# Revit family: PRD_FrankeWS_DspslChts_CHRONOSWasteDisposalChute_E-BS602E
name_source: partatom
category: Specialty Equipment
revit_build: Autodesk Revit 2018 (Build: 20190510_1515(x64)
units: mm (PartAtom-declared; Revit-internal decimal feet)

## family parameters
Cut with Voids When Loaded = No
Host = Face
OmniClass Number = 23.45.05.14.99
OmniClass Title = Other Sanitary Washing Plumbing Fixtures
Part Type = Normal
Room Calculation Point = No
Round Connector Dimension = Use Diameter
Shared = No

## types (1)
- E-BS602E
    AssetType = Fixed
    BIMObjectName = PRD_AR_DisposalChutes_CHRONOSWasteDisposalChute_E-BS602E
    Category = Pr_65_12_70_22, Disposal chutes
    Default Elevation = 1000 mm  [stored 3.28084 ft]
    Description = Waste disposal barrel for table top mounting, stainless steel, visible surfaces satin finished, with raised edge, opening with 127 mm inner diameter, without waste container.
    DurationUnit = year
    Features = stainless steel, visible surfaces satin finished
    Finish = satin finish
    GrossWeight = 0.69 kg
    IfcExportAs = IfcSanitaryTerminalType
    IfcExportType = USERDEFINED
    MainColor = stainless steel
    MainMaterial = PRD_AR_StainlessSteel_SatinFinished
    Manufacturer = KWC Group AG
    ManufacturerName = KWC Group AG
    ManufacturerURL = www.kwc.com
    Material = Stainless steel
    Model = E-BS602E
    ModelNumber = 2000101106
    ModelReference = E-BS602E
    NBSDescription = Disposal chutes
    NBSReference = 45-30-15/310
    Name = CHRONOS Waste disposal chute E-BS602E
    NetWeight = 0.49 kg
    NominalDepth = 150 mm
    NominalHeight = 120 mm  [stored 0.393701 ft]
    NominalLength = 0 mm  [stored 0 ft]
    NominalWidth = 0 mm  [stored 0 ft]
    ProductInformation = https://pim.kwc.com
    Quantity = 1
    QuantityUom = Piece
    Shape = cylinder
    Size = 150 x 120 mm (D x H)
    Status = New
    TypeOfMounting = Table top mounting
    URL = www.kwc.com
    Uniclass2015Code = Pr_65_12_70_22
    Uniclass2015Title = Disposal chutes
    Uniclass2015Version = Products v1.23
    Version = 1
    WarrantyDurationUnit = year

note: [stored X ft] marks values corroborated as IEEE doubles in the binary element streams (Revit-internal decimal feet)

## geometry (parser evidence)
native form markers: Sweep x3
no freeform markers — native parametric forms only
